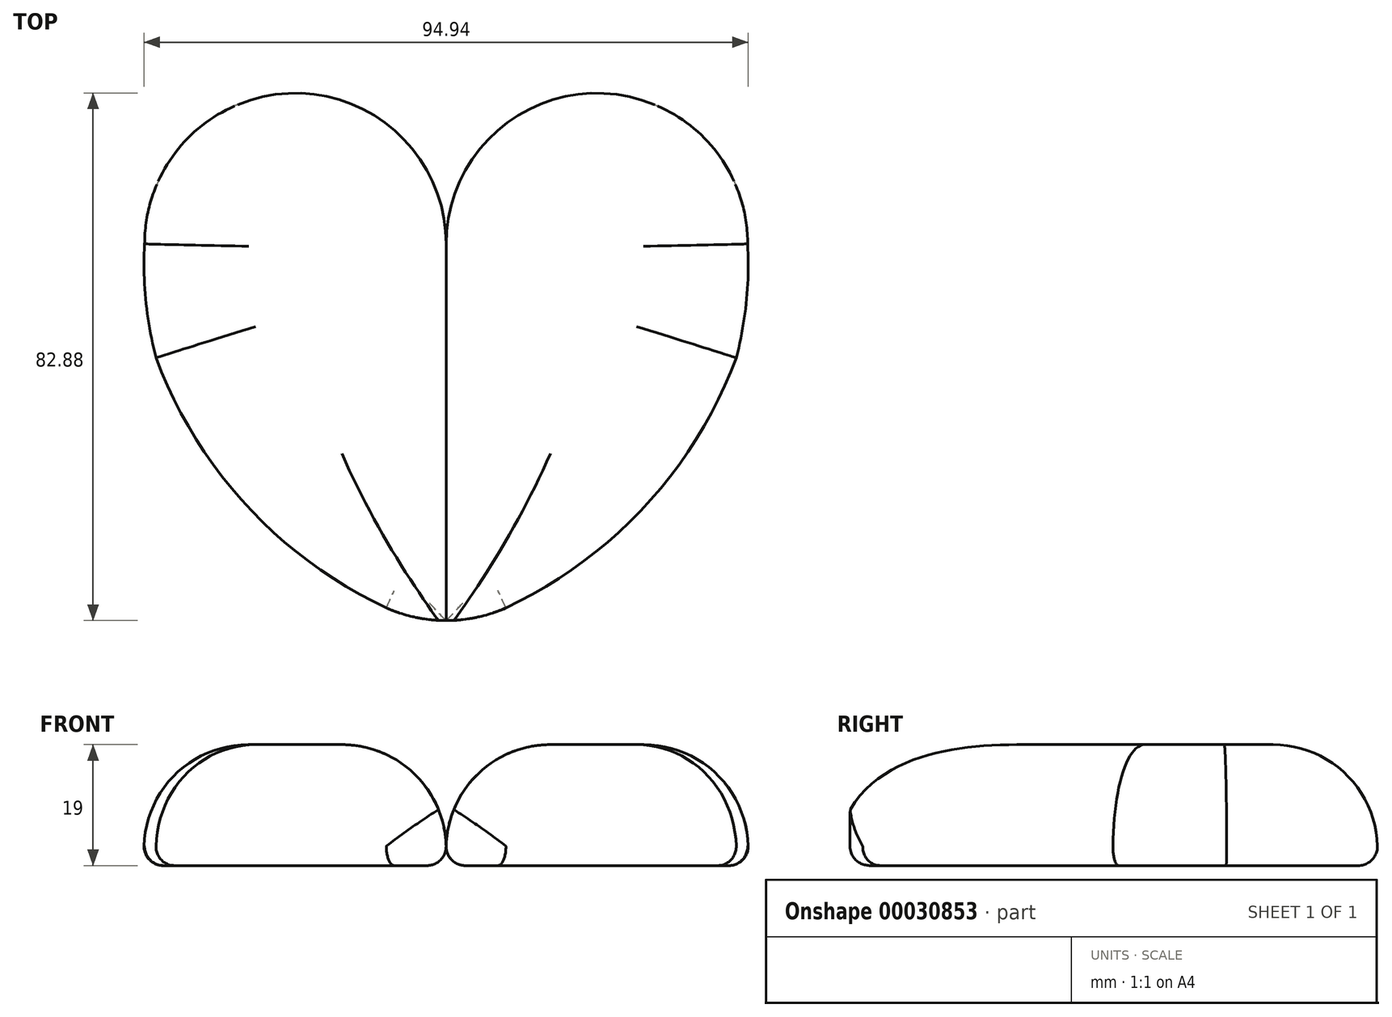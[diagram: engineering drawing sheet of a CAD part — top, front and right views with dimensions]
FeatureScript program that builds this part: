
annotation { "Feature Type Name" : "Feature", "Feature Type Description" : "" }
export const myFeature = defineFeature(function(context is Context, id is Id, definition is map)
    precondition{}
    {
        {
            var Q0;
            Q0=qCreatedBy(makeId("Top.planeOp"),FACE);
            var sketch = newSketch(context, id + "F0", { "sketchPlane" : qUnion([Q0])});
            skLineSegment(sketch, "E0", {"start": v(0, 17.89) * mm, "end": v(0, -41.3) * mm});
            skArc(sketch, "E1", {"start": v(0, -41.3) * mm, "mid": v(4.98, -40.76) * mm, "end": v(9.73, -39.16) * mm});
            skArc(sketch, "E2", {"start": v(9.73, -39.16) * mm, "mid": v(31.48, -23.08) * mm, "end": v(45.6, 0) * mm});
            skArc(sketch, "E3", {"start": v(45.6, 0) * mm, "mid": v(47.18, 8.87) * mm, "end": v(47.39, 17.89) * mm});
            skArc(sketch, "E4", {"start": v(47.39, 17.89) * mm, "mid": v(23.7, 41.58) * mm, "end": v(0, 17.89) * mm});
            skSolve(sketch);
        }
        {
            var Q0;
            {var subQ2=sQuery(id+"F0.wireOp",EDGE,"E1");Q0=makeQuery(id+"F0.imprint","IMPRINT",FACE,{"disambiguationData":[TD([[makeQuery(id+"F0.imprint","IMPRINT",EDGE,{"derivedFrom":subQ2}),1.0]])]});}
            extrude(context, id + "F1", {"entities" : qUnion([Q0]), "depth" : 19 * mm});
        }
        {
            var Q0;
            Q0=makeQuery(id+"F1.opExtrude","CAP_EDGE",EDGE,{"disambiguationData":[OSD([sQuery(id+"F0.wireOp",EDGE,"E4")])],"isStart":false});
            var Q1;
            Q1=makeQuery(id+"F1.opExtrude","CAP_EDGE",EDGE,{"disambiguationData":[OSD([sQuery(id+"F0.wireOp",EDGE,"E3")])],"isStart":false});
            var Q2;
            Q2=makeQuery(id+"F1.opExtrude","CAP_EDGE",EDGE,{"disambiguationData":[OSD([sQuery(id+"F0.wireOp",EDGE,"E2")])],"isStart":false});
            var Q3;
            Q3=makeQuery(id+"F1.opExtrude","CAP_EDGE",EDGE,{"disambiguationData":[OSD([sQuery(id+"F0.wireOp",EDGE,"E1")])],"isStart":false});
            var Q4;
            {var subQ0=sQuery(id+"F0.wireOp",EDGE,"E0");Q4=makeQuery(id+"F1.opExtrude","CAP_EDGE",EDGE,{"disambiguationData":[OSD([subQ0]),TDD([makeQuery(id+"F0.imprint","IMPRINT",EDGE,{"disambiguationData":[TD([[makeQuery(id+"F0.imprint","INTERSECT",VERTEX,{"derivedFrom":[subQ0,sQuery(id+"F0.wireOp",EDGE,"E4")]}),-1.0]])],"derivedFrom":subQ0})])],"isStart":false});}
            var Q5;
            Q5=makeQuery(id+"F1.opExtrude","CAP_EDGE",EDGE,{"disambiguationData":[OSD([sQuery(id+"F0.wireOp",EDGE,"ca5d9487-3bd5-4562-a4d6-7bd6156ffbd0.5")])],"isStart":false});
            fillet(context, id + "F2", {"entities" : qUnion([Q0, Q1, Q2, Q3, Q4, Q5]), "radius" : 16.38 * mm, "tangentPropagation" : true, "allowEdgeOverflow" : false});
        }
        {
            var Q0;
            Q0=makeQuery(id+"F1.opExtrude","CAP_FACE",FACE,{"disambiguationData":[OSD([sQuery(id+"F0.wireOp",EDGE,"E0"),sQuery(id+"F0.wireOp",EDGE,"E1"),sQuery(id+"F0.wireOp",EDGE,"E2"),sQuery(id+"F0.wireOp",EDGE,"E3"),sQuery(id+"F0.wireOp",EDGE,"E4")])],"isStart":true});
            fillet(context, id + "F3", {"entities" : qUnion([Q0]), "radius" : 3 * mm, "tangentPropagation" : true, "allowEdgeOverflow" : false});
        }
        {
            var Q0;
            Q0=makeQuery(id+"F1.opExtrude","SWEPT_BODY",BODY,{"disambiguationData":[OSD([sQuery(id+"F0.wireOp",EDGE,"E0"),sQuery(id+"F0.wireOp",EDGE,"E1"),sQuery(id+"F0.wireOp",EDGE,"E2"),sQuery(id+"F0.wireOp",EDGE,"E3"),sQuery(id+"F0.wireOp",EDGE,"E4"),sQuery(id+"F0.wireOp",EDGE,"ca5d9487-3bd5-4562-a4d6-7bd6156ffbd0.0"),sQuery(id+"F0.wireOp",EDGE,"ca5d9487-3bd5-4562-a4d6-7bd6156ffbd0.1"),sQuery(id+"F0.wireOp",EDGE,"ca5d9487-3bd5-4562-a4d6-7bd6156ffbd0.2"),sQuery(id+"F0.wireOp",EDGE,"ca5d9487-3bd5-4562-a4d6-7bd6156ffbd0.3"),sQuery(id+"F0.wireOp",EDGE,"ca5d9487-3bd5-4562-a4d6-7bd6156ffbd0.4"),sQuery(id+"F0.wireOp",EDGE,"ca5d9487-3bd5-4562-a4d6-7bd6156ffbd0.5")])]});
            var Q1;
            Q1=qCreatedBy(makeId("Right.planeOp"),FACE);
            mirror(context, id + "F4", {"entities" : qUnion([Q0]), "mirrorPlane" : qUnion([Q1])});
        }
    });
